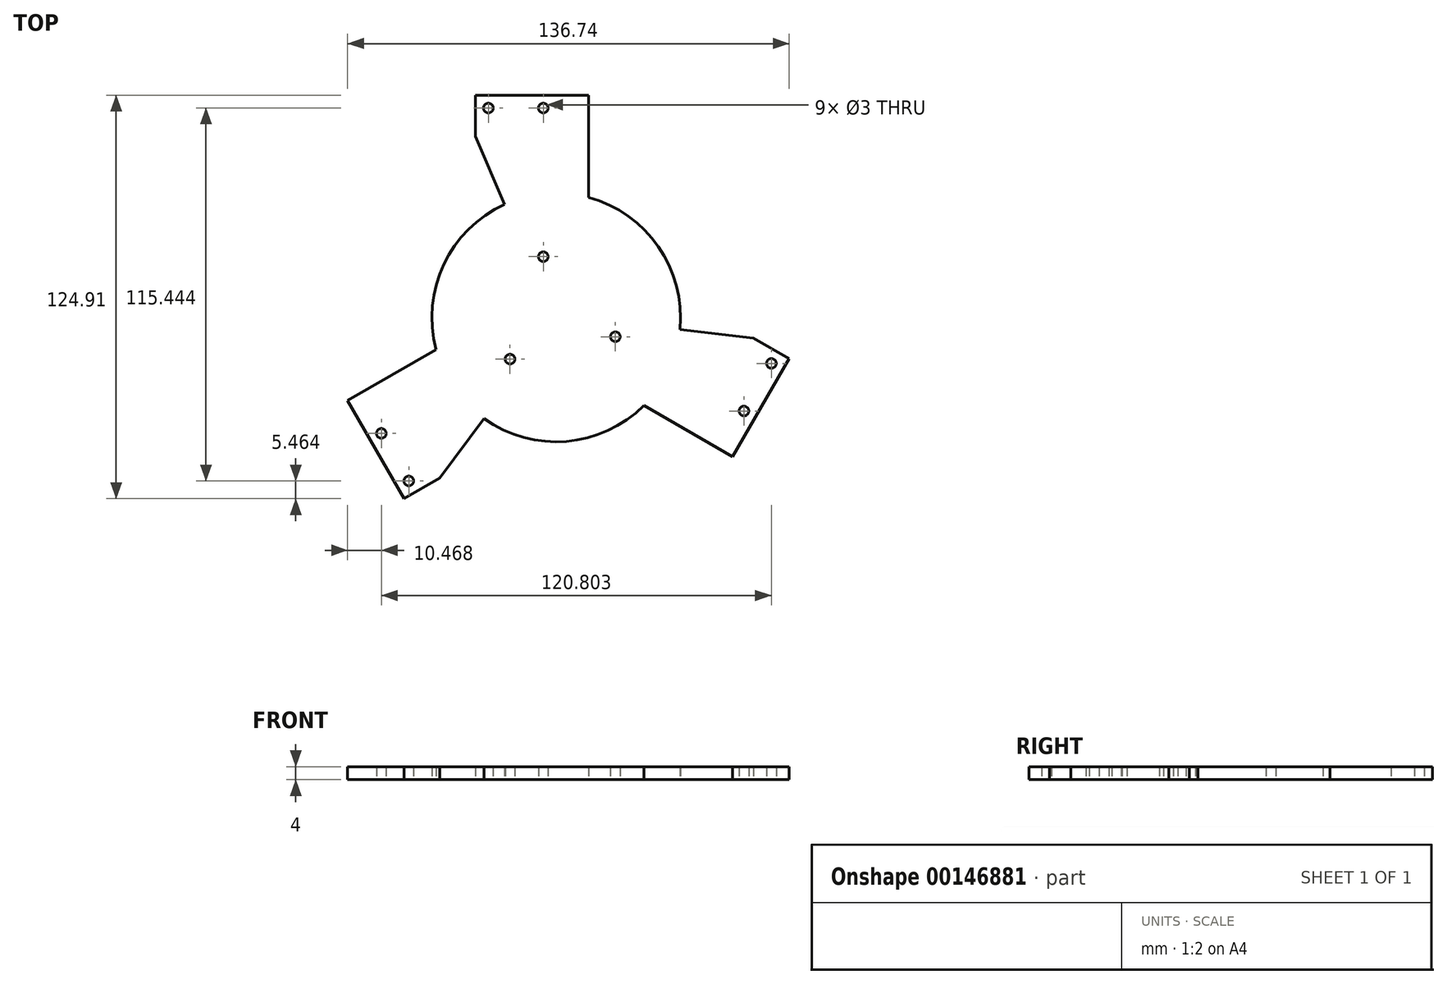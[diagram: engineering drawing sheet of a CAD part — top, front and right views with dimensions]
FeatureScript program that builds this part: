
annotation { "Feature Type Name" : "Feature", "Feature Type Description" : "" }
export const myFeature = defineFeature(function(context is Context, id is Id, definition is map)
    precondition{}
    {
        {
            var Q0;
            Q0=qCreatedBy(makeId("Top.planeOp"),FACE);
            var sketch = newSketch(context, id + "F0", { "sketchPlane" : qUnion([Q0])});
            skCircle(sketch, "E0", {"center": v(-4, 64.84) * mm, "radius": 1.5 * mm});
            skCircle(sketch, "E1", {"center": v(-21, 64.84) * mm, "radius": 1.5 * mm});
            skCircle(sketch, "E2", {"center": v(-4, 18.84) * mm, "radius": 1.5 * mm});
            skLineSegment(sketch, "E3", {"start": v(-25, 68.84) * mm, "end": v(10, 68.84) * mm});
            skLineSegment(sketch, "E4", {"start": v(10, 68.84) * mm, "end": v(10, 59.16) * mm});
            skLineSegment(sketch, "E5", {"start": v(-15.95, 35.03) * mm, "end": v(-25, 56.05) * mm});
            skLineSegment(sketch, "E6", {"start": v(-25, 56.05) * mm, "end": v(-25, 68.84) * mm});
            skCircle(sketch, "E7.1.0", {"center": v(-45.65, -50.6) * mm, "radius": 1.5 * mm});
            skCircle(sketch, "E7.1.1", {"center": v(-54.15, -35.88) * mm, "radius": 1.5 * mm});
            skLineSegment(sketch, "E7.1.2", {"start": v(-64.62, -25.76) * mm, "end": v(-56.23, -20.92) * mm});
            skLineSegment(sketch, "E7.1.3", {"start": v(-22.36, -31.32) * mm, "end": v(-29.24, -40.56) * mm});
            skLineSegment(sketch, "E7.1.4", {"start": v(-47.12, -56.07) * mm, "end": v(-64.62, -25.76) * mm});
            skCircle(sketch, "E7.1.5", {"center": v(-14.31, -12.88) * mm, "radius": 1.5 * mm});
            skLineSegment(sketch, "E7.1.6", {"start": v(-36.04, -49.67) * mm, "end": v(-47.12, -56.07) * mm});
            skCircle(sketch, "E7.2.0", {"center": v(66.65, -14.23) * mm, "radius": 1.5 * mm});
            skCircle(sketch, "E7.2.1", {"center": v(58.15, -28.96) * mm, "radius": 1.5 * mm});
            skLineSegment(sketch, "E7.2.2", {"start": v(54.62, -43.08) * mm, "end": v(46.23, -38.24) * mm});
            skLineSegment(sketch, "E7.2.3", {"start": v(38.3, -3.7) * mm, "end": v(49.74, -5.05) * mm});
            skLineSegment(sketch, "E7.2.4", {"start": v(72.12, -12.77) * mm, "end": v(54.62, -43.08) * mm});
            skCircle(sketch, "E7.2.5", {"center": v(18.31, -5.96) * mm, "radius": 1.5 * mm});
            skLineSegment(sketch, "E7.2.6", {"start": v(61.04, -6.37) * mm, "end": v(72.12, -12.77) * mm});
            skPoint(sketch, "E7.center", {"position": v(0, 0) * mm});
            skLineSegment(sketch, "E8.trimOffspring", {"start": v(-47.43, -15.83) * mm, "end": v(-37.19, -9.92) * mm});
            skLineSegment(sketch, "E9.trimOffspring", {"start": v(37.43, -33.16) * mm, "end": v(27.19, -27.24) * mm});
            skLineSegment(sketch, "E10.trimOffspring", {"start": v(10, 59.16) * mm, "end": v(10, 37.16) * mm});
            skLineSegment(sketch, "E11", {"start": v(-56.23, -20.92) * mm, "end": v(-47.43, -15.83) * mm});
            skLineSegment(sketch, "E12", {"start": v(-36.04, -49.67) * mm, "end": v(-29.24, -40.56) * mm});
            skLineSegment(sketch, "E13", {"start": v(46.23, -38.24) * mm, "end": v(37.43, -33.16) * mm});
            skLineSegment(sketch, "E14", {"start": v(61.04, -6.37) * mm, "end": v(49.74, -5.05) * mm});
            skArc(sketch, "E15", {"start": v(-22.36, -31.32) * mm, "mid": v(3.16, -38.36) * mm, "end": v(27.19, -27.24) * mm});
            skArc(sketch, "E16.trimOffspring", {"start": v(-15.95, 35.03) * mm, "mid": v(-34.8, 16.44) * mm, "end": v(-37.19, -9.92) * mm});
            skArc(sketch, "E17.trimOffspring", {"start": v(38.3, -3.7) * mm, "mid": v(31.64, 21.91) * mm, "end": v(10, 37.16) * mm});
            skSolve(sketch);
        }
        {
            var Q0;
            Q0 = qSketchRegion(id + "F0", true);
            extrude(context, id + "F1", {"entities" : qUnion([Q0]), "depth" : 4 * mm});
        }
    });
